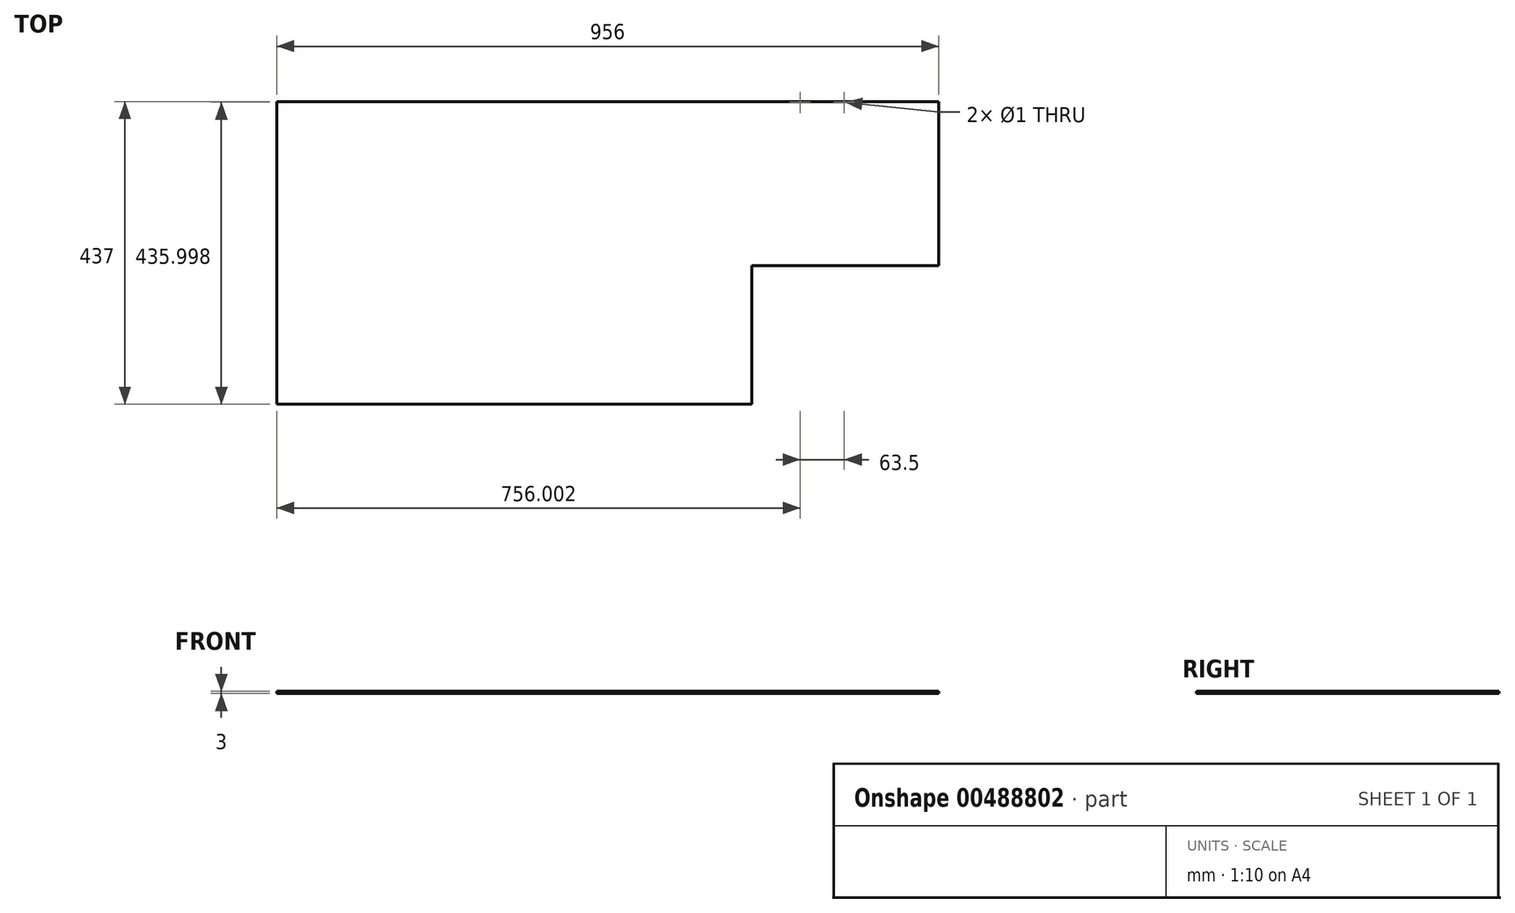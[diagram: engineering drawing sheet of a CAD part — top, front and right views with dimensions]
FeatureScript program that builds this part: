
annotation { "Feature Type Name" : "Feature", "Feature Type Description" : "" }
export const myFeature = defineFeature(function(context is Context, id is Id, definition is map)
    precondition{}
    {
        {
            var Q0;
            Q0=qCreatedBy(makeId("Top.planeOp"),FACE);
            var sketch = newSketch(context, id + "F0", { "sketchPlane" : qUnion([Q0])});
            skLineSegment(sketch, "E0.bottom", {"start": v(-491.1, 185.52) * mm, "end": v(464.9, 185.52) * mm});
            skLineSegment(sketch, "E0.top", {"start": v(-491.1, -251.48) * mm, "end": v(194.9, -251.48) * mm});
            skLineSegment(sketch, "E0.left", {"start": v(-491.1, 185.52) * mm, "end": v(-491.1, -251.48) * mm});
            skLineSegment(sketch, "E0.right", {"start": v(464.9, 185.52) * mm, "end": v(464.9, -51.48) * mm});
            skLineSegment(sketch, "E1.top", {"start": v(464.9, -51.48) * mm, "end": v(194.9, -51.48) * mm});
            skLineSegment(sketch, "E1.right", {"start": v(194.9, -251.48) * mm, "end": v(194.9, -51.48) * mm});
            skLineSegment(sketch, "E2", {"start": v(464.9, 185.52) * mm, "end": v(264.9, 185.52) * mm});
            skLineSegment(sketch, "E3", {"start": v(264.9, 185.52) * mm, "end": v(201.4, 185.52) * mm});
            skLineSegment(sketch, "E4", {"start": v(264.9, 185.52) * mm, "end": v(328.4, 185.52) * mm});
            skLineSegment(sketch, "E5", {"start": v(264.9, 185.52) * mm, "end": v(264.9, 136.56) * mm});
            skLineSegment(sketch, "E6", {"start": v(328.4, 185.52) * mm, "end": v(328.4, 133.43) * mm});
            skCircle(sketch, "E7", {"center": v(264.9, 184.52) * mm, "radius": 0.5 * mm});
            skCircle(sketch, "E8", {"center": v(328.4, 184.52) * mm, "radius": 0.5 * mm});
            skSolve(sketch);
        }
        {
            var Q0;
            Q0=makeQuery(id+"F0.imprint","IMPRINT",FACE,{"disambiguationData":[TD([[makeQuery(id+"F0.imprint","IMPRINT",EDGE,{"derivedFrom":sQuery(id+"F0.wireOp",EDGE,"E0.bottom")}),-1.0]])]});
            extrude(context, id + "F1", {"entities" : qUnion([Q0]), "depth" : 3 * mm});
        }
        {
            var Q0;
            Q0 = qSketchRegion(id + "F0", true);
            extrude(context, id + "F2", {"entities" : qUnion([Q0]), "operationType" : NewBodyOperationType.REMOVE, "oppositeDirection" : true, "depth" : 25 * mm, "offsetDistance" : 25 * mm});
        }
    });
